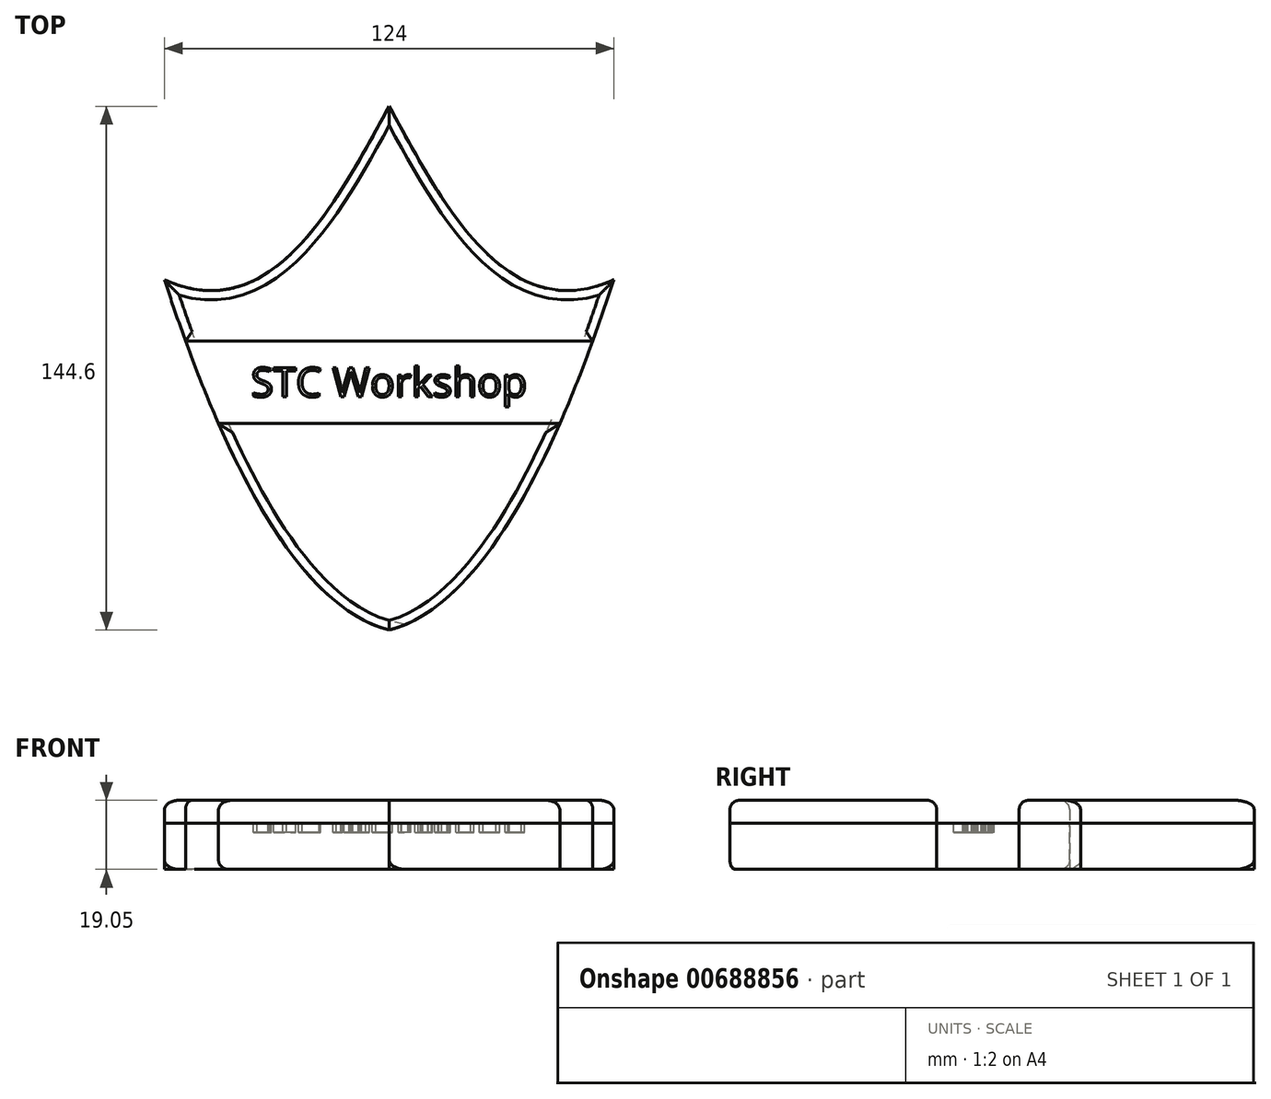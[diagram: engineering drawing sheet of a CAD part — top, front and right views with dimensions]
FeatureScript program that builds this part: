
annotation { "Feature Type Name" : "Feature", "Feature Type Description" : "" }
export const myFeature = defineFeature(function(context is Context, id is Id, definition is map)
    precondition{}
    {
        {
            var Q0;
            Q0=qCreatedBy(makeId("Top.planeOp"),FACE);
            var sketch = newSketch(context, id + "F0", { "sketchPlane" : qUnion([Q0])});
            skFitSpline(sketch, "E0", {"points": [v(-62, 25.12) * mm, v(0, -71.6) * mm], "startDerivative": vector(49.5, -151.4) * mm, "endDerivative": vector(75.37, -19.4) * mm});
            skFitSpline(sketch, "E1", {"points": [v(-62, 25.12) * mm, v(0, 73) * mm], "startDerivative": vector(89.28, -40.76) * mm, "endDerivative": vector(43.35, 79.58) * mm});
            skFitSpline(sketch, "E2.MirrorCS", {"points": [v(62, 25.12) * mm, v(0, -71.6) * mm], "startDerivative": vector(-49.5, -151.4) * mm, "endDerivative": vector(-75.37, -19.4) * mm});
            skFitSpline(sketch, "E3.MirrorCS", {"points": [v(62, 25.12) * mm, v(0, 73) * mm], "startDerivative": vector(-89.28, -40.76) * mm, "endDerivative": vector(-43.35, 79.58) * mm});
            skLineSegment(sketch, "E4", {"start": v(-56.16, 8.19) * mm, "end": v(56.16, 8.19) * mm});
            skLineSegment(sketch, "E5", {"start": v(-47.06, -14.6) * mm, "end": v(47.06, -14.6) * mm});
            skSolve(sketch);
        }
        {
            var Q0;
            {var subQ3=sQuery(id+"F0.wireOp",EDGE,"E1");Q0=makeQuery(id+"F0.imprint","IMPRINT",FACE,{"disambiguationData":[TD([[makeQuery(id+"F0.imprint","IMPRINT",EDGE,{"derivedFrom":subQ3}),-1.0]])]});}
            var Q1;
            {var subQ3=sQuery(id+"F0.wireOp",EDGE,"E5");Q1=makeQuery(id+"F0.imprint","IMPRINT",FACE,{"disambiguationData":[TD([[makeQuery(id+"F0.imprint","IMPRINT",EDGE,{"derivedFrom":subQ3}),-1.0]])]});}
            extrude(context, id + "F1", {"entities" : qUnion([Q0, Q1]), "depth" : 19.05 * mm, "offsetDistance" : 25.4 * mm});
        }
        {
            var Q0;
            Q0 = qSketchRegion(id + "F0", true);
            extrude(context, id + "F2", {"entities" : qUnion([Q0]), "depth" : 12.7 * mm, "offsetDistance" : 25.4 * mm});
        }
        {
            var Q0;
            Q0=makeQuery(id+"F2.opExtrude","CAP_FACE",FACE,{"disambiguationData":[OSD([sQuery(id+"F0.wireOp",EDGE,"E0"),sQuery(id+"F0.wireOp",EDGE,"E1"),sQuery(id+"F0.wireOp",EDGE,"E2.MirrorCS"),sQuery(id+"F0.wireOp",EDGE,"E3.MirrorCS")])],"isStart":false});
            var sketch = newSketch(context, id + "F3", { "sketchPlane" : qUnion([Q0])});
            skText(sketch, "E6", { "text": "STC Workshop", "fontName": "OpenSans-Regular.ttf"});
            const initialGuessF3  = {"E6": [-0.0381, -0.00722, 1, 0, 0.0081]};
            skSetInitialGuess(sketch, initialGuessF3);
            skSolve(sketch);
        }
        {
            var Q0;
            Q0 = qSketchRegion(id + "F3", true);
            extrude(context, id + "F4", {"entities" : qUnion([Q0]), "operationType" : NewBodyOperationType.REMOVE, "oppositeDirection" : true, "depth" : 2.54 * mm, "offsetDistance" : 25.4 * mm});
        }
        {
            var Q0;
            Q0=makeQuery(id+"F1.opExtrude","CAP_FACE",FACE,{"disambiguationData":[OSD([sQuery(id+"F0.wireOp",EDGE,"E0"),sQuery(id+"F0.wireOp",EDGE,"E1"),sQuery(id+"F0.wireOp",EDGE,"E2.MirrorCS"),sQuery(id+"F0.wireOp",EDGE,"E3.MirrorCS"),sQuery(id+"F0.wireOp",EDGE,"E4")])],"isStart":false});
            var Q1;
            Q1=makeQuery(id+"F1.opExtrude","CAP_FACE",FACE,{"disambiguationData":[OSD([sQuery(id+"F0.wireOp",EDGE,"E0"),sQuery(id+"F0.wireOp",EDGE,"E2.MirrorCS"),sQuery(id+"F0.wireOp",EDGE,"E5")])],"isStart":false});
            var Q2;
            {var subQ0=sQuery(id+"F0.wireOp",EDGE,"E0");Q2=makeQuery(id+"F1.opExtrude","CAP_EDGE",EDGE,{"disambiguationData":[OSD([subQ0]),TDD([makeQuery(id+"F0.imprint","IMPRINT",EDGE,{"disambiguationData":[TD([[makeQuery(id+"F0.imprint","INTERSECT",VERTEX,{"derivedFrom":[subQ0,sQuery(id+"F0.wireOp",EDGE,"E2.MirrorCS")]}),1.0]])],"derivedFrom":subQ0})])],"isStart":true});}
            var Q3;
            Q3=makeQuery(id+"F2.opExtrude","CAP_EDGE",EDGE,{"disambiguationData":[OSD([sQuery(id+"F0.wireOp",EDGE,"E2.MirrorCS")])],"isStart":true});
            var Q4;
            Q4=makeQuery(id+"F2.opExtrude","CAP_EDGE",EDGE,{"disambiguationData":[OSD([sQuery(id+"F0.wireOp",EDGE,"E3.MirrorCS")])],"isStart":true});
            var Q5;
            Q5=makeQuery(id+"F2.opExtrude","CAP_EDGE",EDGE,{"disambiguationData":[OSD([sQuery(id+"F0.wireOp",EDGE,"E1")])],"isStart":true});
            var Q6;
            Q6=makeQuery(id+"F2.opExtrude","CAP_EDGE",EDGE,{"disambiguationData":[OSD([sQuery(id+"F0.wireOp",EDGE,"E0")])],"isStart":true});
            fillet(context, id + "F5", {"entities" : qUnion([Q0, Q1, Q2, Q3, Q4, Q5, Q6]), "radius" : 2.54 * mm, "tangentPropagation" : true, "allowEdgeOverflow" : false});
        }
    });
